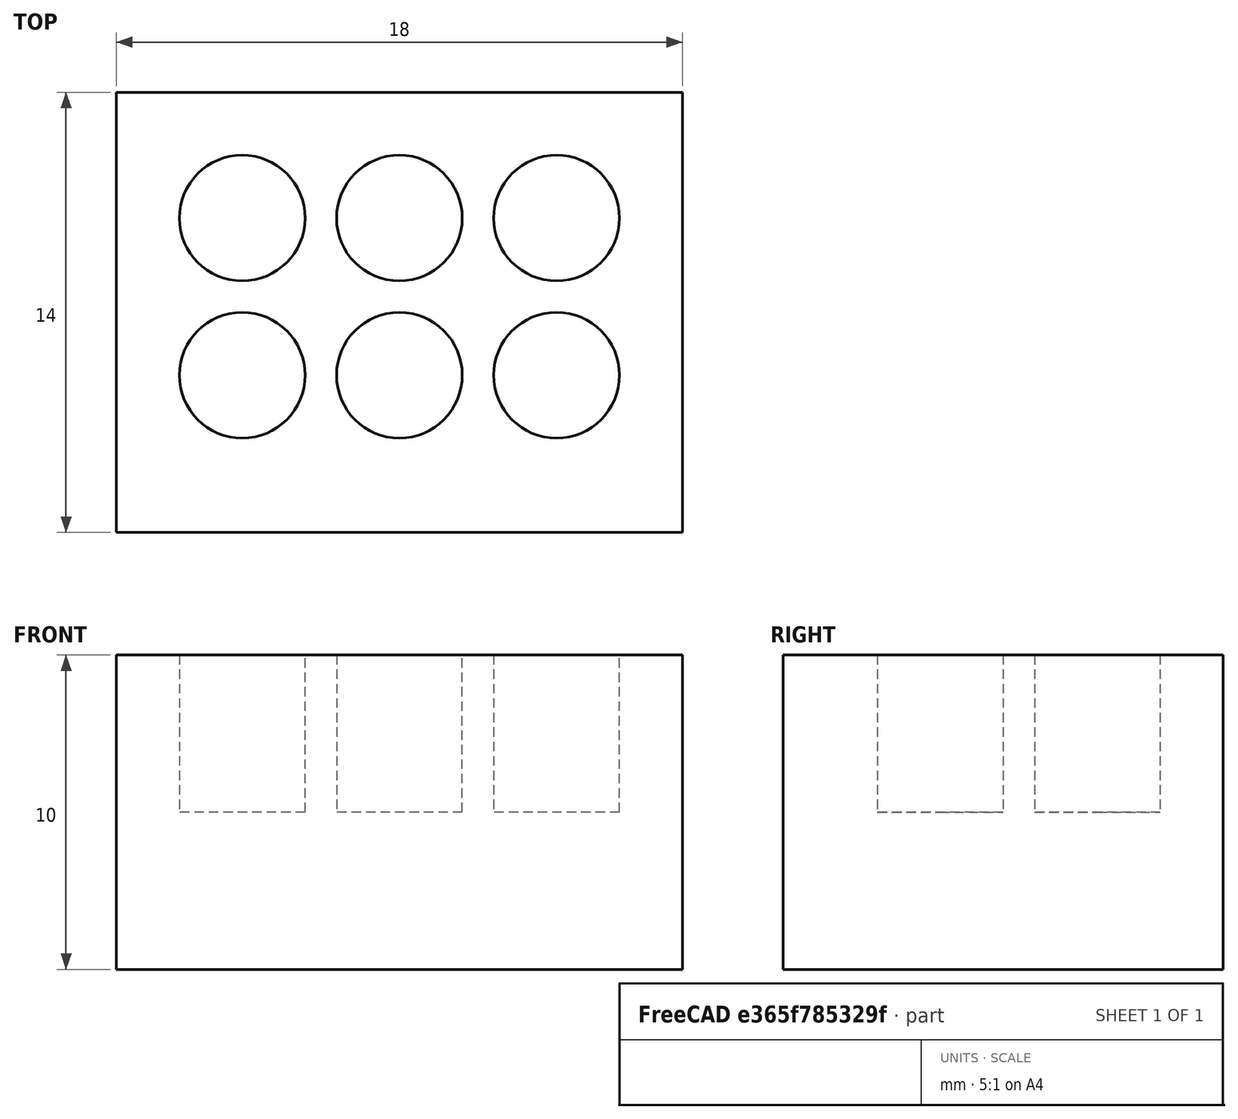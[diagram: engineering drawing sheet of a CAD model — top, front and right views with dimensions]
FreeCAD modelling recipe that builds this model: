
FCSTD DOCUMENT  (FreeCAD 0.21R33694 (Git))
Label: OJT1_T09R08_mao
License: All rights reserved
LicenseURL: http://en.wikipedia.org/wiki/All_rights_reserved
objects: Part::Cylinder×6, Part::MultiFuse×1, Part::Box×1, Part::Cut×1
note: 9 computed .brp shape members not serialized (recipe doc carries the construction recipe); baked Part::Feature solids carry a one-line shape summary decoded from their .brp

FEATURE [Part::Cylinder] Cylinder  label="cilindre1"
  Angle = 360
  AttacherType = Attacher::AttachEngine3D
  FirstAngle = 0
  Height = 10
  Placement = pos=(0,0,5) rot=(0,0,1;0rad)
  Radius = 2
  SecondAngle = 0
FEATURE [Part::Cylinder] Cylinder001  label="cilindre2"
  Angle = 360
  AttacherType = Attacher::AttachEngine3D
  FirstAngle = 0
  Height = 10
  Placement = pos=(0,5,5) rot=(0,0,1;0rad)
  Radius = 2
  SecondAngle = 0
FEATURE [Part::Cylinder] Cylinder002  label="cilindre3"
  Angle = 360
  AttacherType = Attacher::AttachEngine3D
  FirstAngle = 0
  Height = 10
  Placement = pos=(5,5,5) rot=(0,0,1;0rad)
  Radius = 2
  SecondAngle = 0
FEATURE [Part::Cylinder] Cylinder003  label="cilindre4"
  Angle = 360
  AttacherType = Attacher::AttachEngine3D
  FirstAngle = 0
  Height = 10
  Placement = pos=(5,0,5) rot=(0,0,1;0rad)
  Radius = 2
  SecondAngle = 0
FEATURE [Part::Cylinder] Cylinder004  label="cilindre5"
  Angle = 360
  AttacherType = Attacher::AttachEngine3D
  FirstAngle = 0
  Height = 10
  Placement = pos=(10,0,5) rot=(0,0,1;0rad)
  Radius = 2
  SecondAngle = 0
FEATURE [Part::Cylinder] Cylinder005  label="cilindre6"
  Angle = 360
  AttacherType = Attacher::AttachEngine3D
  FirstAngle = 0
  Height = 10
  Placement = pos=(10,5,5) rot=(0,0,1;0rad)
  Radius = 2
  SecondAngle = 0
FEATURE [Part::MultiFuse] Fusion  label="forats"
  Refine = true
  Shapes = -> [Cylinder,Cylinder001,Cylinder002,Cylinder003,Cylinder004,Cylinder005]
FEATURE [Part::Box] Box  label="base"
  AttacherType = Attacher::AttachEngine3D
  Height = 10
  Length = 18
  Placement = pos=(-4,-5,0) rot=(0,0,1;0rad)
  Width = 14
FEATURE [Part::Cut] Cut
  Base = -> Box
  Refine = true
  Tool = -> Fusion
